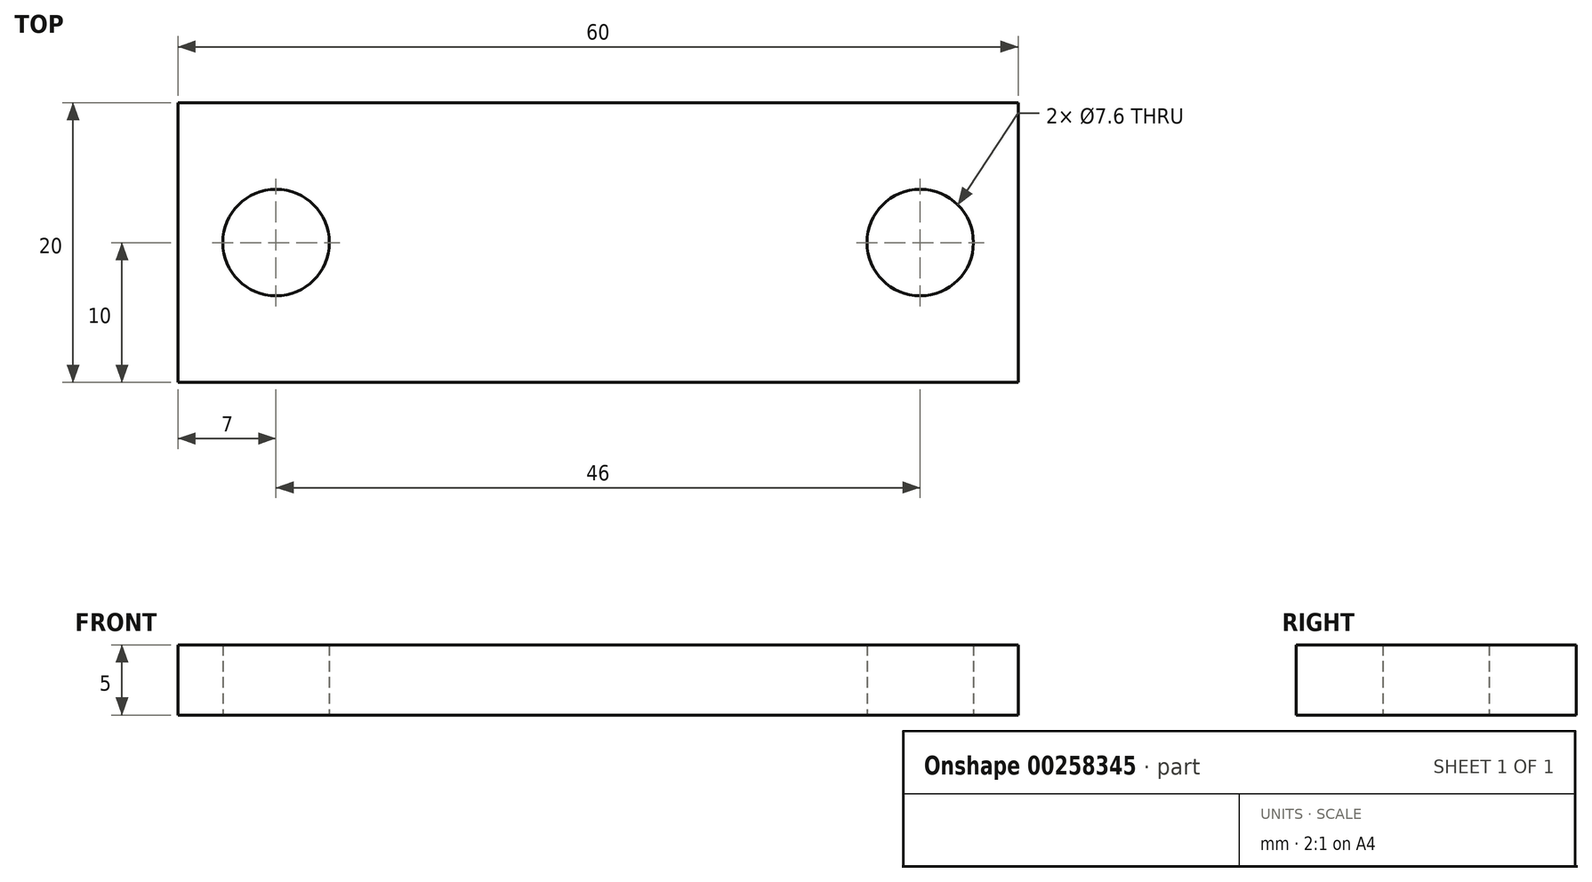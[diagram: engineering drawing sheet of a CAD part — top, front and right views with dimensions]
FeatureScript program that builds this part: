
annotation { "Feature Type Name" : "Feature", "Feature Type Description" : "" }
export const myFeature = defineFeature(function(context is Context, id is Id, definition is map)
    precondition{}
    {
        {
            var Q0;
            Q0=qCreatedBy(makeId("Top.planeOp"),FACE);
            var sketch = newSketch(context, id + "F0", { "sketchPlane" : qUnion([Q0])});
            skLineSegment(sketch, "E0.bottom", {"start": v(30, -10) * mm, "end": v(-30, -10) * mm});
            skLineSegment(sketch, "E0.top", {"start": v(30, 10) * mm, "end": v(-30, 10) * mm});
            skLineSegment(sketch, "E0.left", {"start": v(30, -10) * mm, "end": v(30, 10) * mm});
            skLineSegment(sketch, "E0.right", {"start": v(-30, -10) * mm, "end": v(-30, 10) * mm});
            skPoint(sketch, "E0.middle", {"position": v(0, 0) * mm});
            skLineSegment(sketch, "E1", {"start": v(-30, 0) * mm, "end": v(30, 0) * mm, "construction": true});
            skCircle(sketch, "E2", {"center": v(-23, 0) * mm, "radius": 3.8 * mm});
            skCircle(sketch, "E3", {"center": v(23, 0) * mm, "radius": 3.8 * mm});
            skLineSegment(sketch, "E4", {"start": v(0, 10) * mm, "end": v(0, -10) * mm, "construction": true});
            skSolve(sketch);
        }
        {
            var Q0;
            Q0=qSketchRegion(id+"F0",true);
            extrude(context, id + "F1", {"entities" : qUnion([Q0]), "depth" : 5 * mm});
        }
    });
